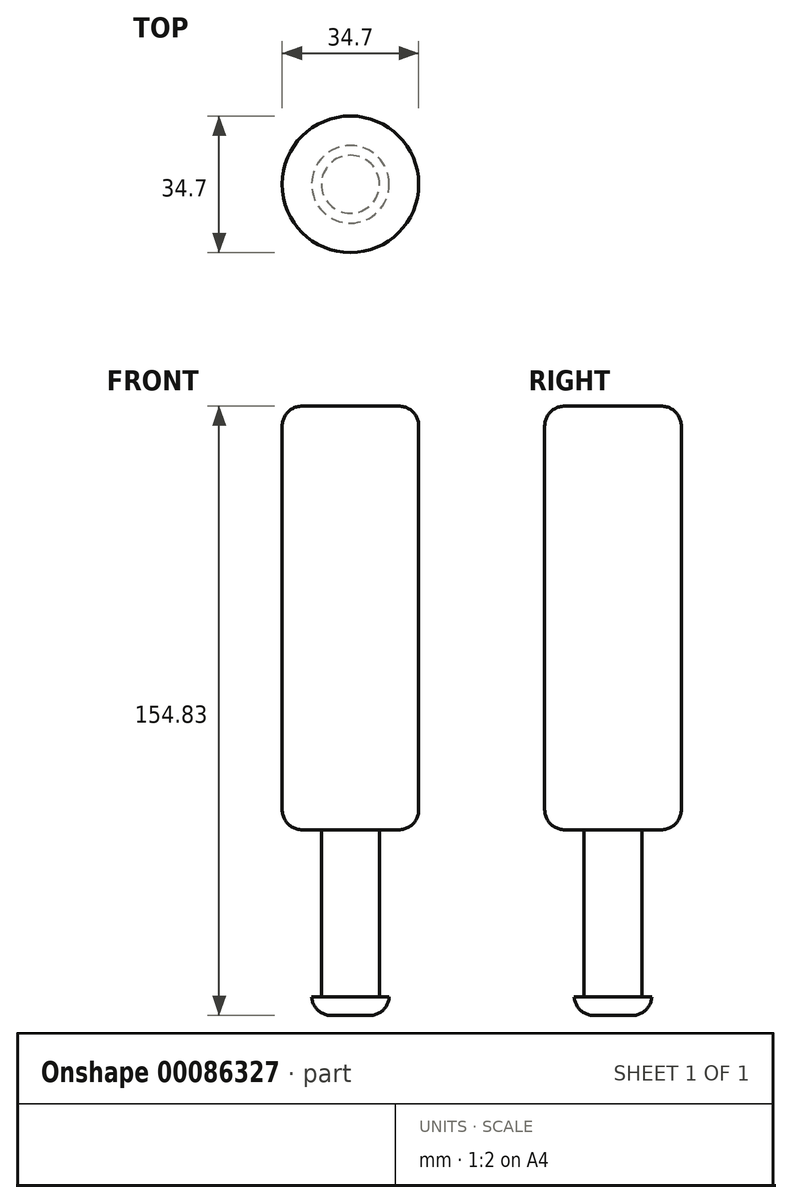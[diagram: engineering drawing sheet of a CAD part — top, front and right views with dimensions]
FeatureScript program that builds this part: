
annotation { "Feature Type Name" : "Feature", "Feature Type Description" : "" }
export const myFeature = defineFeature(function(context is Context, id is Id, definition is map)
    precondition{}
    {
        {
            var Q0;
            Q0=qCreatedBy(makeId("Top.planeOp"),FACE);
            var sketch = newSketch(context, id + "F0", { "sketchPlane" : qUnion([Q0])});
            skCircle(sketch, "E0", {"center": v(0, 0) * mm, "radius": 17.35 * mm});
            skSolve(sketch);
        }
        {
            var Q0;
            Q0=makeQuery(id+"F0.imprint","IMPRINT",FACE,{"disambiguationData":[TD([[makeQuery(id+"F0.imprint","IMPRINT",EDGE,{"derivedFrom":sQuery(id+"F0.wireOp",EDGE,"E0")}),1.0]])]});
            extrude(context, id + "F1", {"entities" : qUnion([Q0]), "depth" : 107.63 * mm});
        }
        {
            var Q0;
            Q0=makeQuery(id+"F1.opExtrude","CAP_EDGE",EDGE,{"disambiguationData":[OSD([sQuery(id+"F0.wireOp",EDGE,"E0")])],"isStart":false});
            fillet(context, id + "F2", {"entities" : qUnion([Q0]), "radius" : 5.08 * mm, "tangentPropagation" : true, "allowEdgeOverflow" : false});
        }
        {
            var Q0;
            Q0=makeQuery(id+"F1.opExtrude","CAP_EDGE",EDGE,{"disambiguationData":[OSD([sQuery(id+"F0.wireOp",EDGE,"E0")])],"isStart":true});
            fillet(context, id + "F3", {"entities" : qUnion([Q0]), "radius" : 5.08 * mm, "tangentPropagation" : true, "allowEdgeOverflow" : false});
        }
        {
            var Q0;
            Q0=qCreatedBy(makeId("Top.planeOp"),FACE);
            var sketch = newSketch(context, id + "F4", { "sketchPlane" : qUnion([Q0])});
            skCircle(sketch, "E1", {"center": v(0, 0) * mm, "radius": 7.37 * mm});
            skSolve(sketch);
        }
        {
            var Q0;
            Q0 = qSketchRegion(id + "F4", true);
            extrude(context, id + "F5", {"entities" : qUnion([Q0]), "operationType" : NewBodyOperationType.ADD, "oppositeDirection" : true, "depth" : 42.53 * mm});
        }
        {
            var Q0;
            Q0=makeQuery(id+"F5.opExtrude","CAP_FACE",FACE,{"disambiguationData":[OSD([sQuery(id+"F4.wireOp",EDGE,"E1")])],"isStart":false});
            var sketch = newSketch(context, id + "F6", { "sketchPlane" : qUnion([Q0])});
            skCircle(sketch, "E2", {"center": v(0, 0) * mm, "radius": 9.86 * mm});
            skSolve(sketch);
        }
        {
            var Q0;
            Q0 = qSketchRegion(id + "F6", true);
            extrude(context, id + "F7", {"entities" : qUnion([Q0]), "operationType" : NewBodyOperationType.ADD, "depth" : 4.68 * mm});
        }
        {
            var Q0;
            Q0=makeQuery(id+"F7.opExtrude","CAP_FACE",FACE,{"disambiguationData":[OSD([sQuery(id+"F6.wireOp",EDGE,"E2")])],"isStart":false});
            fillet(context, id + "F8", {"entities" : qUnion([Q0]), "radius" : 5.08 * mm, "tangentPropagation" : true, "allowEdgeOverflow" : false});
        }
    });
